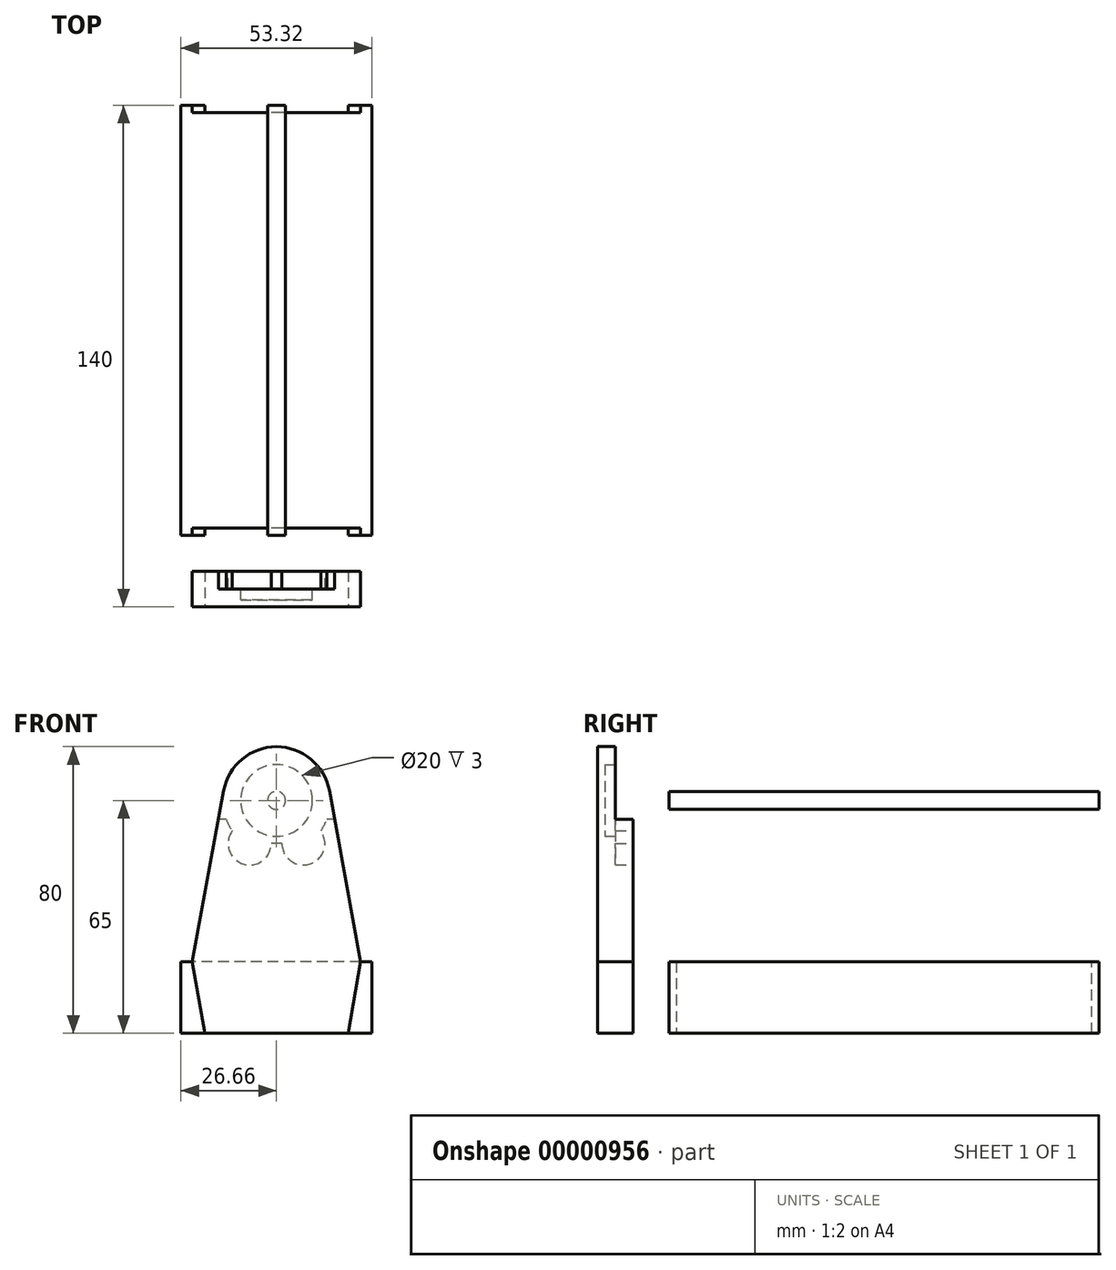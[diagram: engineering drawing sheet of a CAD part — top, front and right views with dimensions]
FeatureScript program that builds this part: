
annotation { "Feature Type Name" : "Feature", "Feature Type Description" : "" }
export const myFeature = defineFeature(function(context is Context, id is Id, definition is map)
    precondition{}
    {
        {
            var Q0;
            Q0=qCreatedBy(makeId("Top.planeOp"),FACE);
            var sketch = newSketch(context, id + "F0", { "sketchPlane" : qUnion([Q0])});
            skLineSegment(sketch, "E0.bottom", {"start": v(26.66, 60) * mm, "end": v(-26.66, 60) * mm});
            skLineSegment(sketch, "E0.top", {"start": v(26.66, -60) * mm, "end": v(-26.66, -60) * mm});
            skLineSegment(sketch, "E0.left", {"start": v(26.66, 60) * mm, "end": v(26.66, -60) * mm});
            skLineSegment(sketch, "E0.right", {"start": v(-26.66, 60) * mm, "end": v(-26.66, -60) * mm});
            skLineSegment(sketch, "E1", {"start": v(0, -60) * mm, "end": v(0, 0) * mm, "construction": true});
            skLineSegment(sketch, "E2", {"start": v(0, 0) * mm, "end": v(-26.66, 0) * mm, "construction": true});
            skSolve(sketch);
        }
        {
            var Q0;
            Q0=makeQuery(id+"F0.imprint","IMPRINT",FACE,{"disambiguationData":[TD([[makeQuery(id+"F0.imprint","IMPRINT",EDGE,{"derivedFrom":sQuery(id+"F0.wireOp",EDGE,"E0.bottom")}),1.0]])]});
            extrude(context, id + "F1", {"entities" : qUnion([Q0]), "depth" : 20 * mm});
        }
        {
            var Q0;
            Q0=makeQuery(id+"F1.opExtrude","SWEPT_FACE",FACE,{"disambiguationData":[OSD([sQuery(id+"F0.wireOp",EDGE,"E0.top")])]});
            cPlane(context, id + "F2", {"entities" : qUnion([Q0]), "cplaneType" : CPlaneType.OFFSET, "offset" : 10 * mm, "width" : 150 * mm, "height" : 150 * mm});
        }
        {
            var Q0;
            Q0=qCreatedBy(id+"F2.planeOp",FACE);
            var sketch = newSketch(context, id + "F3", { "sketchPlane" : qUnion([Q0])});
            skLineSegment(sketch, "E3", {"start": v(-23.5, 0) * mm, "end": v(23.5, 0) * mm});
            skLineSegment(sketch, "E4", {"start": v(23.5, 0) * mm, "end": v(23.5, 120) * mm});
            skLineSegment(sketch, "E5", {"start": v(23.5, 120) * mm, "end": v(-23.5, 120) * mm});
            skLineSegment(sketch, "E6", {"start": v(-23.5, 120) * mm, "end": v(-23.5, 0) * mm});
            skSolve(sketch);
        }
        {
            var Q0;
            Q0=makeQuery(id+"F3.imprint","IMPRINT",FACE,{"disambiguationData":[TD([[makeQuery(id+"F3.imprint","IMPRINT",EDGE,{"derivedFrom":sQuery(id+"F3.wireOp",EDGE,"E3")}),1.0]])]});
            extrude(context, id + "F4", {"entities" : qUnion([Q0]), "depth" : 10 * mm});
        }
        {
            var Q0;
            Q0=makeQuery(id+"F4.opExtrude","CAP_FACE",FACE,{"disambiguationData":[OSD([sQuery(id+"F3.wireOp",EDGE,"E3"),sQuery(id+"F3.wireOp",EDGE,"E4"),sQuery(id+"F3.wireOp",EDGE,"E5"),sQuery(id+"F3.wireOp",EDGE,"E6")])],"isStart":false});
            var sketch = newSketch(context, id + "F5", { "sketchPlane" : qUnion([Q0])});
            skLineSegment(sketch, "E7", {"start": v(0, 0) * mm, "end": v(0, 80) * mm, "construction": true});
            skLineSegment(sketch, "E8", {"start": v(-23.5, 20) * mm, "end": v(-14.75, 67.7) * mm});
            skLineSegment(sketch, "E9", {"start": v(-14.75, 67.7) * mm, "end": v(14.75, 67.7) * mm, "construction": true});
            skLineSegment(sketch, "E10", {"start": v(14.75, 67.7) * mm, "end": v(23.5, 20) * mm});
            skArc(sketch, "E11", {"start": v(14.75, 67.7) * mm, "mid": v(0, 80) * mm, "end": v(-14.75, 67.7) * mm});
            skLineSegment(sketch, "E12", {"start": v(-23.5, 20) * mm, "end": v(-23.5, 120) * mm});
            skLineSegment(sketch, "E13", {"start": v(-23.5, 120) * mm, "end": v(23.5, 120) * mm});
            skLineSegment(sketch, "E14", {"start": v(23.5, 120) * mm, "end": v(23.5, 20) * mm});
            skSolve(sketch);
        }
        {
            var Q0;
            Q0 = qSketchRegion(id + "F5", true);
            extrude(context, id + "F6", {"entities" : qUnion([Q0]), "operationType" : NewBodyOperationType.REMOVE, "oppositeDirection" : true, "depth" : 10 * mm});
        }
        {
            var Q0;
            Q0=makeQuery(id+"F4.opExtrude","CAP_FACE",FACE,{"disambiguationData":[OSD([sQuery(id+"F3.wireOp",EDGE,"E3"),sQuery(id+"F3.wireOp",EDGE,"E4"),sQuery(id+"F3.wireOp",EDGE,"E5"),sQuery(id+"F3.wireOp",EDGE,"E6")])],"isStart":true});
            var sketch = newSketch(context, id + "F7", { "sketchPlane" : qUnion([Q0])});
            skArc(sketch, "E15", {"start": v(-12.37, 56.51) * mm, "mid": v(-9.34, 47.3) * mm, "end": v(-1.5, 53) * mm});
            skArc(sketch, "E16", {"start": v(1.5, 53) * mm, "mid": v(9.34, 47.3) * mm, "end": v(12.37, 56.51) * mm});
            skLineSegment(sketch, "E17", {"start": v(7.5, 53) * mm, "end": v(-7.5, 53) * mm, "construction": true});
            skLineSegment(sketch, "E18", {"start": v(0, 53) * mm, "end": v(0, 65) * mm, "construction": true});
            skArc(sketch, "E19.trimOffspring", {"start": v(12.37, 56.51) * mm, "mid": v(13.3, 58.06) * mm, "end": v(14.03, 59.7) * mm});
            skLineSegment(sketch, "E20", {"start": v(-16.22, 59.7) * mm, "end": v(-14.03, 59.7) * mm});
            skLineSegment(sketch, "E21", {"start": v(16.22, 59.7) * mm, "end": v(14.75, 67.7) * mm});
            skLineSegment(sketch, "E22", {"start": v(-14.75, 67.7) * mm, "end": v(-16.22, 59.7) * mm});
            skArc(sketch, "E23.trimOffspring", {"start": v(-14.03, 59.7) * mm, "mid": v(-13.3, 58.06) * mm, "end": v(-12.37, 56.51) * mm});
            skLineSegment(sketch, "E24.trimOffspring", {"start": v(14.03, 59.7) * mm, "end": v(16.22, 59.7) * mm});
            skArc(sketch, "E25.trimOffspring", {"start": v(14.75, 67.7) * mm, "mid": v(0, 80) * mm, "end": v(-14.75, 67.7) * mm});
            skLineSegment(sketch, "E26", {"start": v(-1.5, 53) * mm, "end": v(1.5, 53) * mm});
            skSolve(sketch);
        }
        {
            var Q0;
            Q0=makeQuery(id+"F7.imprint","IMPRINT",FACE,{"disambiguationData":[TD([[makeQuery(id+"F7.imprint","IMPRINT",EDGE,{"derivedFrom":sQuery(id+"F7.wireOp",EDGE,"E15")}),1.0]])]});
            extrude(context, id + "F8", {"entities" : qUnion([Q0]), "operationType" : NewBodyOperationType.REMOVE, "oppositeDirection" : true, "depth" : 5 * mm});
        }
        {
            var Q0;
            Q0=makeQuery(id+"F8.boolean.opBoolean","COPY",FACE,{"derivedFrom":makeQuery(id+"F8.opExtrude","CAP_FACE",FACE,{"disambiguationData":[OSD([sQuery(id+"F7.wireOp",EDGE,"E15"),sQuery(id+"F7.wireOp",EDGE,"E16"),sQuery(id+"F7.wireOp",EDGE,"E19.trimOffspring"),sQuery(id+"F7.wireOp",EDGE,"E20"),sQuery(id+"F7.wireOp",EDGE,"E21"),sQuery(id+"F7.wireOp",EDGE,"E22"),sQuery(id+"F7.wireOp",EDGE,"E23.trimOffspring"),sQuery(id+"F7.wireOp",EDGE,"E24.trimOffspring"),sQuery(id+"F7.wireOp",EDGE,"E25.trimOffspring"),sQuery(id+"F7.wireOp",EDGE,"E26")])],"isStart":false})});
            var sketch = newSketch(context, id + "F9", { "sketchPlane" : qUnion([Q0])});
            skCircle(sketch, "E27", {"center": v(0, 65) * mm, "radius": 10 * mm});
            skSolve(sketch);
        }
        {
            var Q0;
            Q0 = qSketchRegion(id + "F9", true);
            extrude(context, id + "F10", {"entities" : qUnion([Q0]), "operationType" : NewBodyOperationType.REMOVE, "oppositeDirection" : true, "depth" : 3 * mm});
        }
        {
            var Q0;
            Q0=makeQuery(id+"F1.opExtrude","SWEPT_FACE",FACE,{"disambiguationData":[OSD([sQuery(id+"F0.wireOp",EDGE,"E0.bottom")])]});
            var sketch = newSketch(context, id + "F11", { "sketchPlane" : qUnion([Q0])});
            skCircle(sketch, "E28", {"center": v(0, 65) * mm, "radius": 2.5 * mm});
            skSolve(sketch);
        }
        {
            var Q0;
            Q0 = qSketchRegion(id + "F11", true);
            extrude(context, id + "F12", {"entities" : qUnion([Q0]), "oppositeDirection" : true, "depth" : 120 * mm});
        }
        {
            var Q0;
            Q0=makeQuery(id+"F1.opExtrude","SWEPT_FACE",FACE,{"disambiguationData":[OSD([sQuery(id+"F0.wireOp",EDGE,"E0.top")])]});
            var sketch = newSketch(context, id + "F13", { "sketchPlane" : qUnion([Q0])});
            skLineSegment(sketch, "E29.bottom", {"start": v(-23.5, 20) * mm, "end": v(23.5, 20) * mm});
            skLineSegment(sketch, "E29.top", {"start": v(-19.97, 0) * mm, "end": v(19.97, 0) * mm});
            skLineSegment(sketch, "E29.left", {"start": v(-23.5, 20) * mm, "end": v(-19.97, 0) * mm});
            skLineSegment(sketch, "E29.right", {"start": v(23.5, 20) * mm, "end": v(19.97, 0) * mm});
            skLineSegment(sketch, "E30", {"start": v(0, 0) * mm, "end": v(0, 20) * mm, "construction": true});
            skSolve(sketch);
        }
        {
            var Q0;
            Q0 = qSketchRegion(id + "F13", true);
            extrude(context, id + "F14", {"entities" : qUnion([Q0]), "operationType" : NewBodyOperationType.REMOVE, "oppositeDirection" : true, "depth" : 2 * mm});
        }
        {
            var Q0;
            Q0=makeQuery(id+"F1.opExtrude","SWEPT_FACE",FACE,{"disambiguationData":[OSD([sQuery(id+"F0.wireOp",EDGE,"E0.bottom")])]});
            var sketch = newSketch(context, id + "F15", { "sketchPlane" : qUnion([Q0])});
            skLineSegment(sketch, "E31.bottom", {"start": v(-19.97, 0) * mm, "end": v(19.97, 0) * mm});
            skLineSegment(sketch, "E31.top", {"start": v(-23.5, 20) * mm, "end": v(23.5, 20) * mm});
            skLineSegment(sketch, "E31.left", {"start": v(-19.97, 0) * mm, "end": v(-23.5, 20) * mm});
            skLineSegment(sketch, "E31.right", {"start": v(19.97, 0) * mm, "end": v(23.5, 20) * mm});
            skLineSegment(sketch, "E32", {"start": v(0, 20) * mm, "end": v(0, 0) * mm, "construction": true});
            skSolve(sketch);
        }
        {
            var Q0;
            Q0 = qSketchRegion(id + "F15", true);
            extrude(context, id + "F16", {"entities" : qUnion([Q0]), "operationType" : NewBodyOperationType.REMOVE, "oppositeDirection" : true, "depth" : 2 * mm});
        }
        {
            var Q0;
            Q0=makeQuery(id+"F4.opExtrude","CAP_FACE",FACE,{"disambiguationData":[OSD([sQuery(id+"F3.wireOp",EDGE,"E3"),sQuery(id+"F3.wireOp",EDGE,"E4"),sQuery(id+"F3.wireOp",EDGE,"E5"),sQuery(id+"F3.wireOp",EDGE,"E6")])],"isStart":false});
            var sketch = newSketch(context, id + "F17", { "sketchPlane" : qUnion([Q0])});
            skLineSegment(sketch, "E33", {"start": v(23.5, 20) * mm, "end": v(19.97, 0) * mm});
            skLineSegment(sketch, "E34", {"start": v(19.97, 0) * mm, "end": v(23.5, 0) * mm});
            skLineSegment(sketch, "E35", {"start": v(23.5, 0) * mm, "end": v(23.5, 20) * mm});
            skLineSegment(sketch, "E36", {"start": v(-23.5, 20) * mm, "end": v(-19.97, 0) * mm});
            skLineSegment(sketch, "E37", {"start": v(-19.97, 0) * mm, "end": v(-23.5, 0) * mm});
            skLineSegment(sketch, "E38", {"start": v(-23.5, 0) * mm, "end": v(-23.5, 20) * mm});
            skSolve(sketch);
        }
        {
            var Q0;
            Q0 = qSketchRegion(id + "F17", true);
            extrude(context, id + "F18", {"entities" : qUnion([Q0]), "operationType" : NewBodyOperationType.REMOVE, "oppositeDirection" : true, "depth" : 10 * mm});
        }
    });
